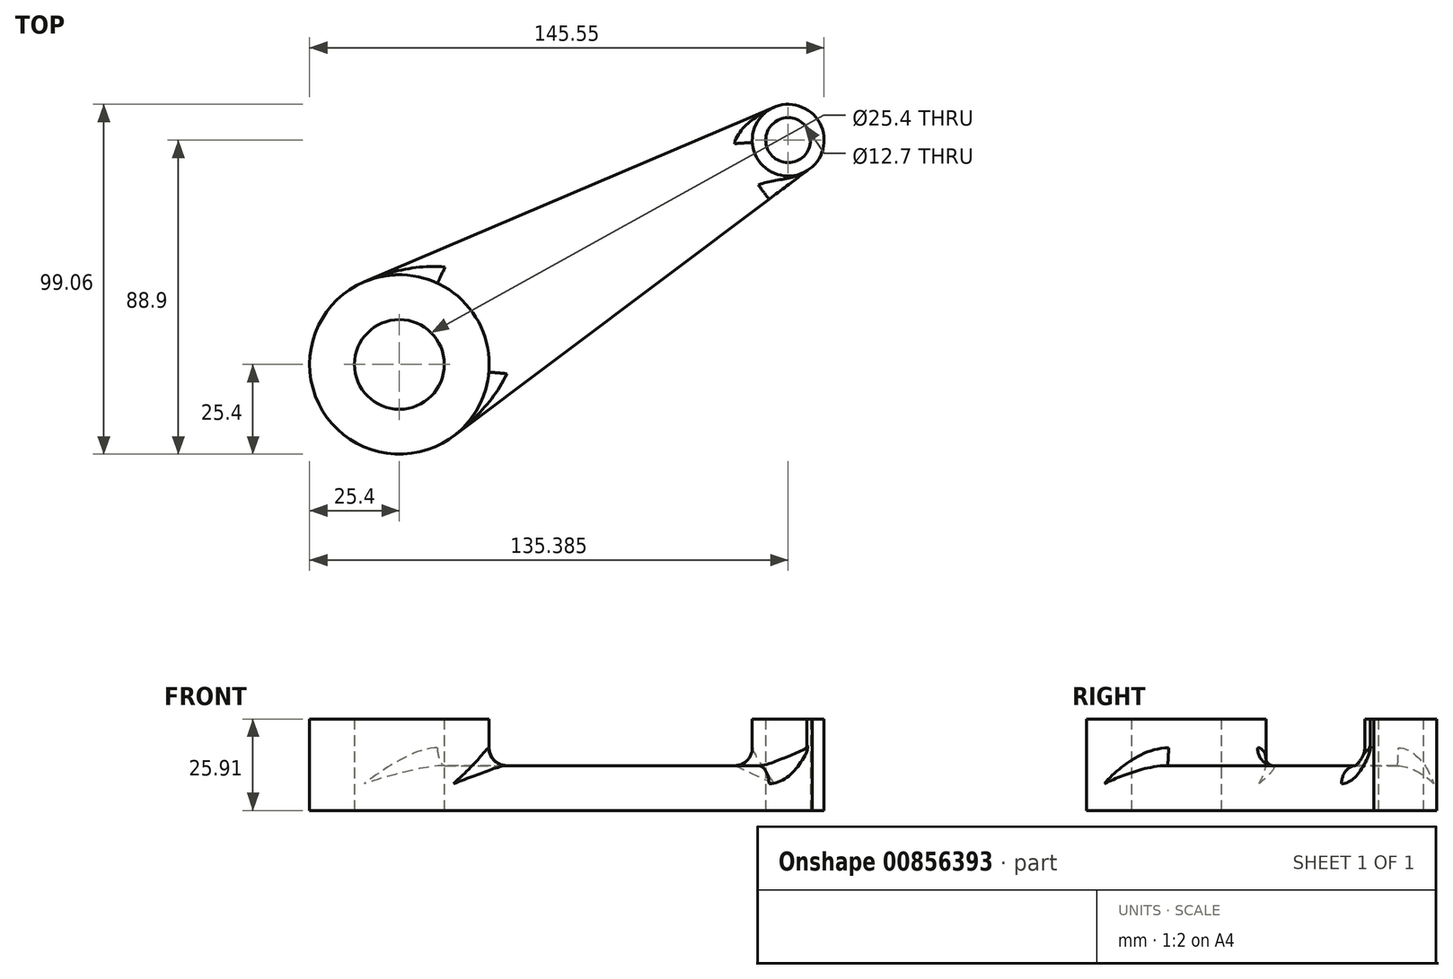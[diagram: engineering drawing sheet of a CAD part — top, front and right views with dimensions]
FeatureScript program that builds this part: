
annotation { "Feature Type Name" : "Feature", "Feature Type Description" : "" }
export const myFeature = defineFeature(function(context is Context, id is Id, definition is map)
    precondition{}
    {
        {
            var Q0;
            Q0=qCreatedBy(makeId("Top.planeOp"),FACE);
            var sketch = newSketch(context, id + "F0", { "sketchPlane" : qUnion([Q0])});
            skLineSegment(sketch, "E0", {"start": v(0, 0) * mm, "end": v(109.99, 63.5) * mm, "construction": true});
            skLineSegment(sketch, "E1", {"start": v(0, 0) * mm, "end": v(127, 0) * mm, "construction": true});
            skCircle(sketch, "E2", {"center": v(0, 0) * mm, "radius": 25.4 * mm});
            skCircle(sketch, "E3", {"center": v(109.99, 63.5) * mm, "radius": 10.16 * mm});
            skLineSegment(sketch, "E4", {"start": v(-9.97, 23.36) * mm, "end": v(106, 72.84) * mm});
            skLineSegment(sketch, "E5", {"start": v(15.25, -20.3) * mm, "end": v(116.8, 55.96) * mm});
            skCircle(sketch, "E6", {"center": v(0, 0) * mm, "radius": 12.7 * mm});
            skCircle(sketch, "E7", {"center": v(109.99, 63.5) * mm, "radius": 6.35 * mm});
            skSolve(sketch);
        }
        {
            var Q0;
            Q0=makeQuery(id+"F0.imprint","IMPRINT",FACE,{"disambiguationData":[TD([[makeQuery(id+"F0.imprint","IMPRINT",EDGE,{"derivedFrom":sQuery(id+"F0.wireOp",EDGE,"E6")}),-1.0]])]});
            var Q1;
            Q1=makeQuery(id+"F0.imprint","IMPRINT",FACE,{"disambiguationData":[TD([[makeQuery(id+"F0.imprint","IMPRINT",EDGE,{"derivedFrom":sQuery(id+"F0.wireOp",EDGE,"E7")}),-1.0]])]});
            extrude(context, id + "F1", {"entities" : qUnion([Q0, Q1]), "depth" : 25.9 * mm, "offsetDistance" : 25.4 * mm});
        }
        {
            var Q0;
            {var subQ0=sQuery(id+"F0.wireOp",EDGE,"E4");Q0=makeQuery(id+"F0.imprint","IMPRINT",FACE,{"disambiguationData":[TD([[makeQuery(id+"F0.imprint","IMPRINT",EDGE,{"derivedFrom":subQ0}),-1.0]])]});}
            extrude(context, id + "F2", {"entities" : qUnion([Q0]), "operationType" : NewBodyOperationType.ADD, "depth" : 12.7 * mm, "offsetDistance" : 25.4 * mm});
        }
        {
            var Q0;
            Q0=makeQuery(id+"F2.opExtrude","CAP_FACE",FACE,{"disambiguationData":[OSD([sQuery(id+"F0.wireOp",EDGE,"E2"),sQuery(id+"F0.wireOp",EDGE,"E3"),sQuery(id+"F0.wireOp",EDGE,"E4"),sQuery(id+"F0.wireOp",EDGE,"E5")])],"isStart":false});
            fillet(context, id + "F3", {"entities" : qUnion([Q0]), "radius" : 5.08 * mm, "tangentPropagation" : true, "allowEdgeOverflow" : false});
        }
    });
